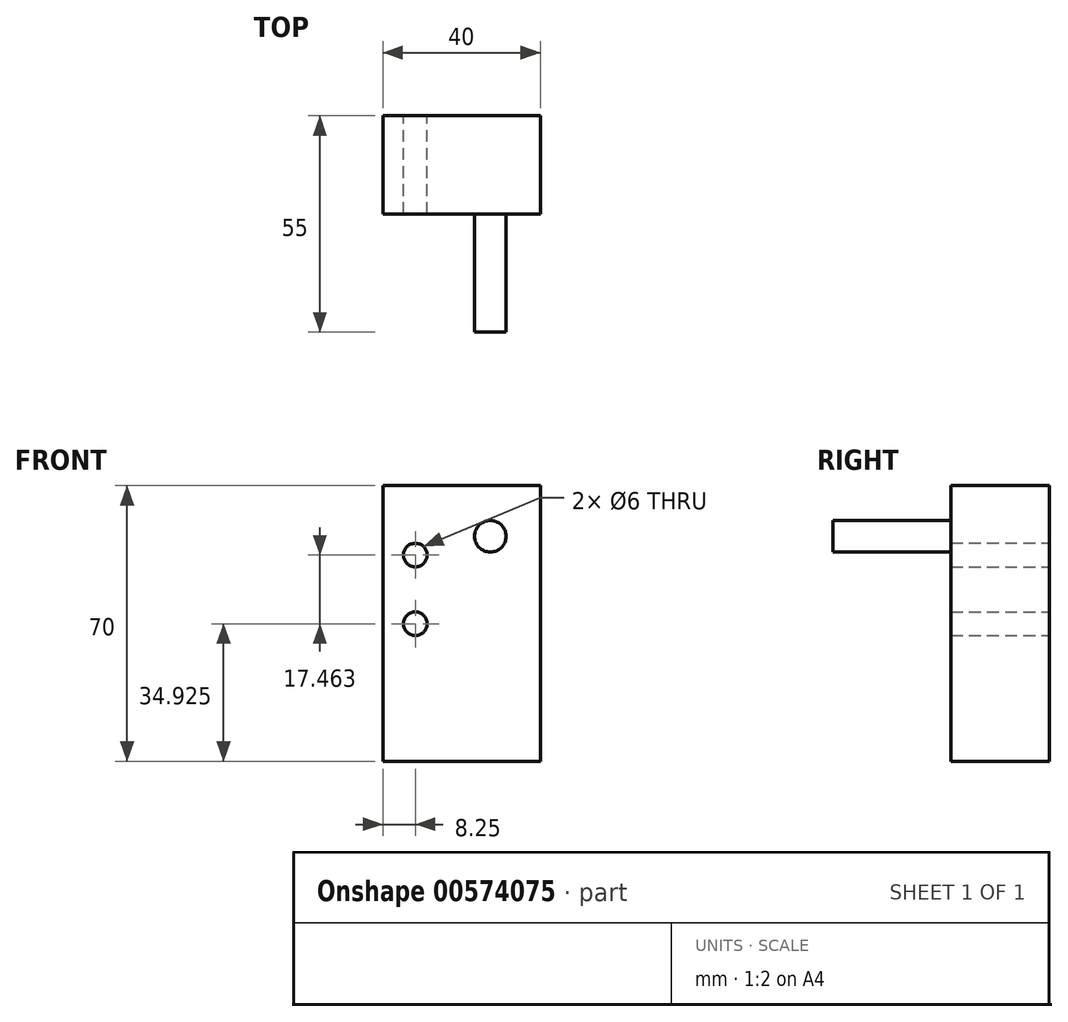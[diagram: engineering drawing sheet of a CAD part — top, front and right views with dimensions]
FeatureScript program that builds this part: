
annotation { "Feature Type Name" : "Feature", "Feature Type Description" : "" }
export const myFeature = defineFeature(function(context is Context, id is Id, definition is map)
    precondition{}
    {
        {
            var Q0;
            Q0=qCreatedBy(makeId("Front.planeOp"),FACE);
            var sketch = newSketch(context, id + "F0", { "sketchPlane" : qUnion([Q0])});
            skLineSegment(sketch, "E0.bottom", {"start": v(40, 70) * mm, "end": v(0, 70) * mm});
            skLineSegment(sketch, "E0.top", {"start": v(40, 0) * mm, "end": v(0, 0) * mm});
            skLineSegment(sketch, "E0.left", {"start": v(40, 70) * mm, "end": v(40, 0) * mm});
            skLineSegment(sketch, "E0.right", {"start": v(0, 70) * mm, "end": v(0, 0) * mm});
            skSolve(sketch);
        }
        {
            var Q0;
            Q0=makeQuery(id+"F0.imprint","IMPRINT",FACE,{"disambiguationData":[TD([[makeQuery(id+"F0.imprint","IMPRINT",EDGE,{"derivedFrom":sQuery(id+"F0.wireOp",EDGE,"E0.bottom")}),1.0]])]});
            extrude(context, id + "F1", {"entities" : qUnion([Q0]), "depth" : 25 * mm, "offsetDistance" : 25 * mm});
        }
        {
            var Q0;
            Q0=makeQuery(id+"F1.opExtrude","CAP_FACE",FACE,{"disambiguationData":[OSD([sQuery(id+"F0.wireOp",EDGE,"E0.bottom"),sQuery(id+"F0.wireOp",EDGE,"E0.top"),sQuery(id+"F0.wireOp",EDGE,"E0.left"),sQuery(id+"F0.wireOp",EDGE,"E0.right")])],"isStart":false});
            var sketch = newSketch(context, id + "F2", { "sketchPlane" : qUnion([Q0])});
            skCircle(sketch, "E1", {"center": v(27.3, 57.15) * mm, "radius": 4 * mm});
            skSolve(sketch);
        }
        {
            var Q0;
            Q0 = qSketchRegion(id + "F2", true);
            extrude(context, id + "F3", {"entities" : qUnion([Q0]), "operationType" : NewBodyOperationType.ADD, "depth" : 30 * mm, "offsetDistance" : 25 * mm});
        }
        {
            var Q0;
            Q0=qCreatedBy(makeId("Front.planeOp"),FACE);
            var sketch = newSketch(context, id + "F4", { "sketchPlane" : qUnion([Q0])});
            skCircle(sketch, "E2", {"center": v(-21.86, 146.07) * mm, "radius": 46.5 * mm});
            skSolve(sketch);
        }
        {
            var Q0;
            Q0=qCreatedBy(makeId("Front.planeOp"),FACE);
            var sketch = newSketch(context, id + "F5", { "sketchPlane" : qUnion([Q0])});
            skCircle(sketch, "E3", {"center": v(8.25, 34.92) * mm, "radius": 3 * mm});
            skCircle(sketch, "E4", {"center": v(8.25, 52.39) * mm, "radius": 3 * mm});
            skSolve(sketch);
        }
        {
            var Q0;
            Q0=sQuery(id+"F5.wireOp",VERTEX,"E4.center");
            var Q1;
            Q1=sQuery(id+"F5.wireOp",VERTEX,"E3.center");
            var Q2;
            Q2=makeQuery(id+"F1.opExtrude","SWEPT_BODY",BODY,{"disambiguationData":[OSD([sQuery(id+"F0.wireOp",EDGE,"E0.bottom"),sQuery(id+"F0.wireOp",EDGE,"E0.top"),sQuery(id+"F0.wireOp",EDGE,"E0.left"),sQuery(id+"F0.wireOp",EDGE,"E0.right")])]});
            hole(context, id + "F6", {"style" : HoleStyle.SIMPLE, "endStyle" : HoleEndStyle.THROUGH, "oppositeDirection" : true, "holeDiameter" : 6 * mm, "isTappedThrough" : true, "tappedDepth" : 12 * mm, "tapClearance" : 3, "locations" : qUnion([Q0, Q1]), "scope" : qUnion([Q2])});
        }
        {
            var Q0;
            Q0=sQuery(id+"F4.wireOp",EDGE,"E2");
            extrude(context, id + "F7", {"bodyType" : ToolBodyType.SURFACE, "surfaceEntities" : qUnion([Q0]), "depth" : 50 * mm, "offsetDistance" : 25 * mm});
        }
    });
